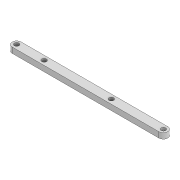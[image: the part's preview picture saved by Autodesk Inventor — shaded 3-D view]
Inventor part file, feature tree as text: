
AUTODESK INVENTOR PART (.ipt)
format: ipt  version: 2022 (Build 260153000, 153)  size: 99,328 bytes
history: native  units: mm
features: extrude x1
ambient origin geometry x8: Origin, YZ Plane, XZ Plane, XY Plane, X Axis, Y Axis, Z Axis, Center Point
bodies: Solid1 (feature_tree)
feature tree (1):
  extrude  "Extrusion1"  Depth=132.801mm
